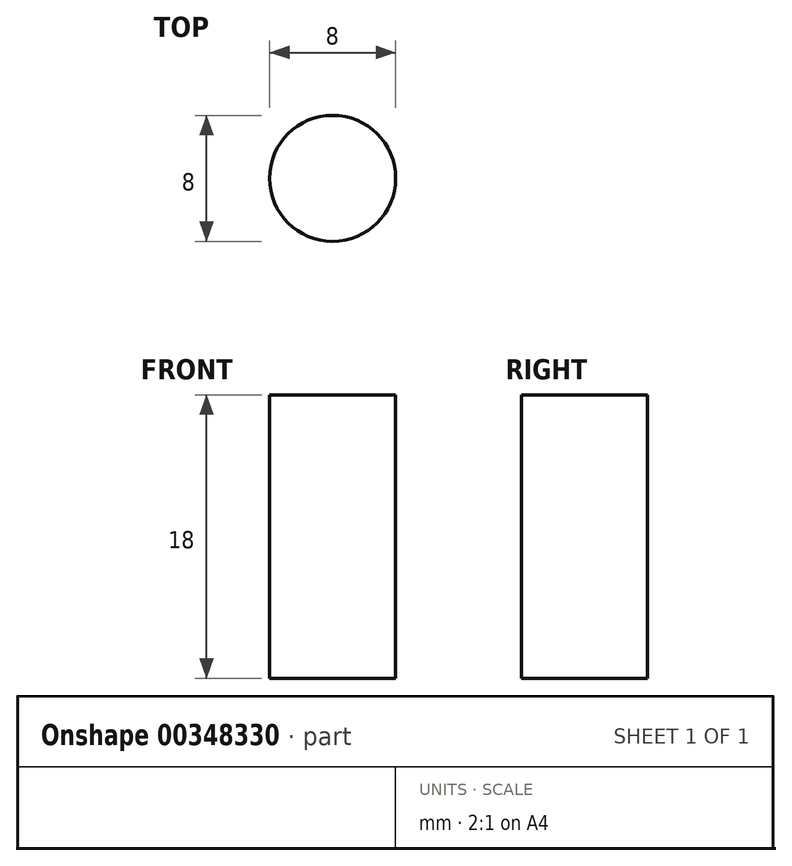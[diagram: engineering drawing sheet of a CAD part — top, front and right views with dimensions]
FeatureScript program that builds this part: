
annotation { "Feature Type Name" : "Feature", "Feature Type Description" : "" }
export const myFeature = defineFeature(function(context is Context, id is Id, definition is map)
    precondition{}
    {
        {
            var Q0;
            Q0=qCreatedBy(makeId("Top.planeOp"),FACE);
            var sketch = newSketch(context, id + "F0", { "sketchPlane" : qUnion([Q0])});
            skCircle(sketch, "E0", {"center": v(0, 0) * mm, "radius": 4 * mm});
            skSolve(sketch);
        }
        {
            var Q0;
            Q0 = qSketchRegion(id + "F0", true);
            extrude(context, id + "F1", {"entities" : qUnion([Q0]), "depth" : 18 * mm});
        }
    });
